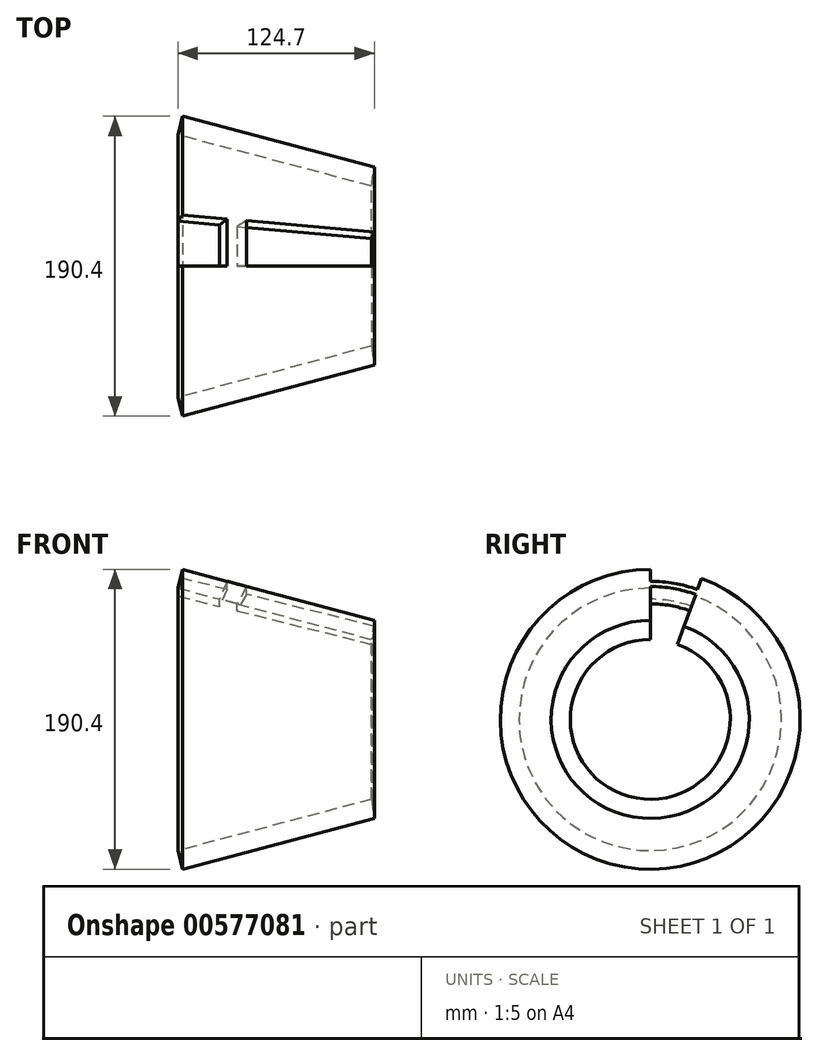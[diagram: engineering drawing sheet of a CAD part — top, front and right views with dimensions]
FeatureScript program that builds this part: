
annotation { "Feature Type Name" : "Feature", "Feature Type Description" : "" }
export const myFeature = defineFeature(function(context is Context, id is Id, definition is map)
    precondition{}
    {
        {
            var Q0;
            Q0=qCreatedBy(makeId("Front.planeOp"),FACE);
            var sketch = newSketch(context, id + "F0", { "sketchPlane" : qUnion([Q0])});
            skLineSegment(sketch, "E0", {"start": v(-51.45, 83.34) * mm, "end": v(71.31, 50.8) * mm});
            skLineSegment(sketch, "E1", {"start": v(-58.35, 0) * mm, "end": v(64.67, 0) * mm});
            skLineSegment(sketch, "E2", {"start": v(73.25, 62.92) * mm, "end": v(-48.53, 95.2) * mm});
            skLineSegment(sketch, "E3", {"start": v(-48.53, 95.2) * mm, "end": v(-51.45, 83.34) * mm});
            skLineSegment(sketch, "E4", {"start": v(73.25, 62.92) * mm, "end": v(71.31, 50.8) * mm});
            skSolve(sketch);
        }
        {
            var Q0;
            Q0=makeQuery(id+"F0.imprint","IMPRINT",FACE,{"disambiguationData":[TD([[makeQuery(id+"F0.imprint","IMPRINT",EDGE,{"derivedFrom":sQuery(id+"F0.wireOp",EDGE,"E0")}),1.0]])]});
            var Q1;
            Q1=sQuery(id+"F0.wireOp",EDGE,"E1");
            revolve(context, id + "F1", {"entities" : qUnion([Q0]), "axis" : qUnion([Q1]), "revolveType" : RevolveType.ONE_DIRECTION, "angle" : 340 * degree});
        }
        {
            var Q0;
            Q0=makeQuery(id+"F1.opRevolve","CAP_FACE",FACE,{"disambiguationData":[OSD([sQuery(id+"F0.wireOp",EDGE,"E0"),sQuery(id+"F0.wireOp",EDGE,"E2"),sQuery(id+"F0.wireOp",EDGE,"E3"),sQuery(id+"F0.wireOp",EDGE,"E4")])],"isStart":false});
            var sketch = newSketch(context, id + "F2", { "sketchPlane" : qUnion([Q0])});
            skLineSegment(sketch, "E5", {"start": v(-20.38, 87.74) * mm, "end": v(-25.22, 76.39) * mm});
            skLineSegment(sketch, "E6", {"start": v(-7.82, 84.4) * mm, "end": v(-13.98, 73.4) * mm});
            skLineSegment(sketch, "E7", {"start": v(-7.82, 84.4) * mm, "end": v(-20.38, 87.74) * mm});
            skLineSegment(sketch, "E8", {"start": v(-13.98, 73.4) * mm, "end": v(-25.22, 76.39) * mm});
            skSolve(sketch);
        }
        {
            var Q0;
            Q0=makeQuery(id+"F2.imprint","IMPRINT",FACE,{"disambiguationData":[TD([[makeQuery(id+"F2.imprint","IMPRINT",EDGE,{"derivedFrom":sQuery(id+"F2.wireOp",EDGE,"E5")}),1.0]])]});
            var Q1;
            Q1=makeQuery(id+"F1.opRevolve","SWEPT_FACE",FACE,{"disambiguationData":[OSD([sQuery(id+"F0.wireOp",EDGE,"E2")])]});
            revolve(context, id + "F3", {"operationType" : NewBodyOperationType.ADD, "entities" : qUnion([Q0]), "axis" : qUnion([Q1]), "revolveType" : RevolveType.FULL});
        }
    });
